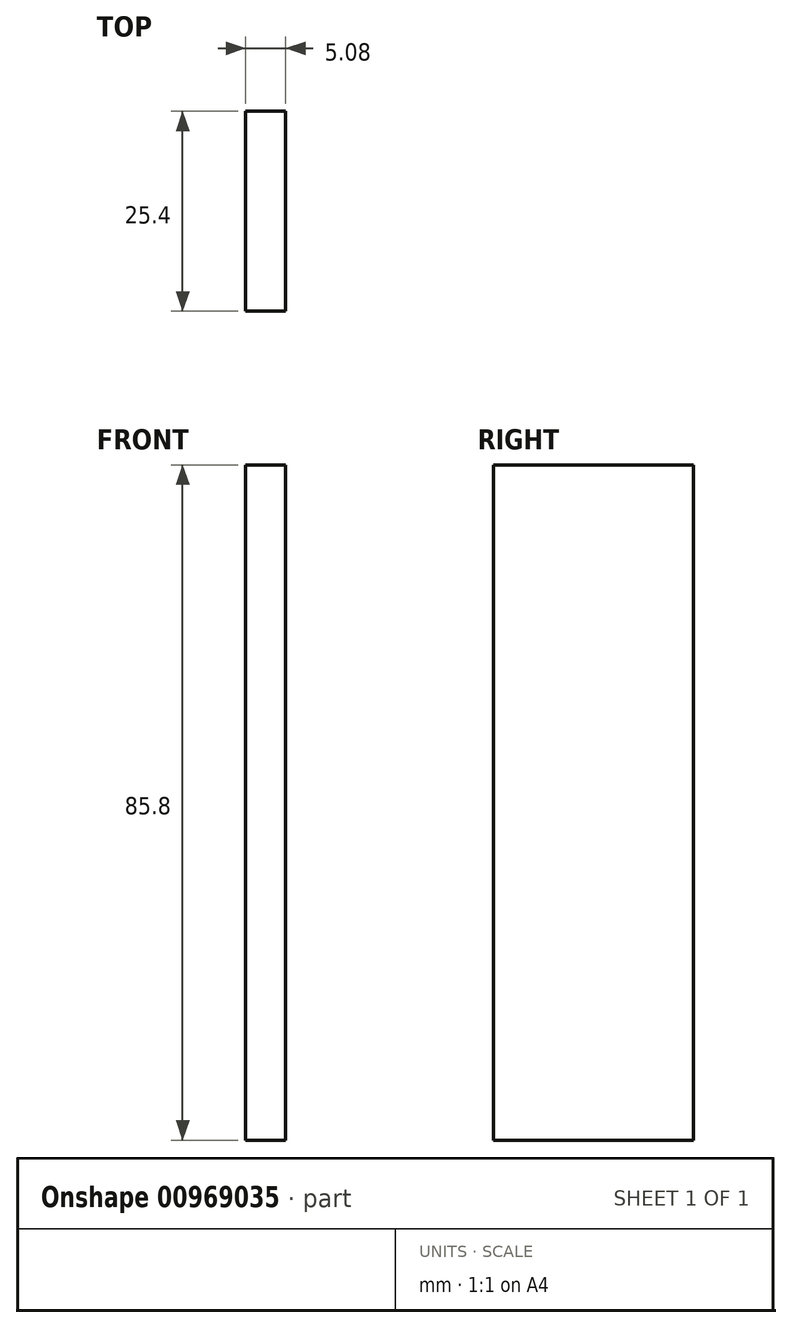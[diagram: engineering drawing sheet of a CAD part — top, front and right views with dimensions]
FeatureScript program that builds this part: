
annotation { "Feature Type Name" : "Feature", "Feature Type Description" : "" }
export const myFeature = defineFeature(function(context is Context, id is Id, definition is map)
    precondition{}
    {
        {
            var Q0;
            Q0=qCreatedBy(makeId("Front.planeOp"),FACE);
            var sketch = newSketch(context, id + "F0", { "sketchPlane" : qUnion([Q0])});
            skLineSegment(sketch, "E0.bottom", {"start": v(2.54, 42.9) * mm, "end": v(-2.54, 42.9) * mm});
            skLineSegment(sketch, "E0.top", {"start": v(2.54, -42.9) * mm, "end": v(-2.54, -42.9) * mm});
            skLineSegment(sketch, "E0.left", {"start": v(2.54, 42.9) * mm, "end": v(2.54, -42.9) * mm});
            skLineSegment(sketch, "E0.right", {"start": v(-2.54, 42.9) * mm, "end": v(-2.54, -42.9) * mm});
            skPoint(sketch, "E0.middle", {"position": v(0, 0) * mm});
            skSolve(sketch);
        }
        {
            var Q0;
            Q0=makeQuery(id+"F0.imprint","IMPRINT",FACE,{"disambiguationData":[TD([[makeQuery(id+"F0.imprint","IMPRINT",EDGE,{"derivedFrom":sQuery(id+"F0.wireOp",EDGE,"E0.bottom")}),1.0]])]});
            extrude(context, id + "F1", {"entities" : qUnion([Q0]), "depth" : 25.4 * mm, "offsetDistance" : 25.4 * mm});
        }
    });
